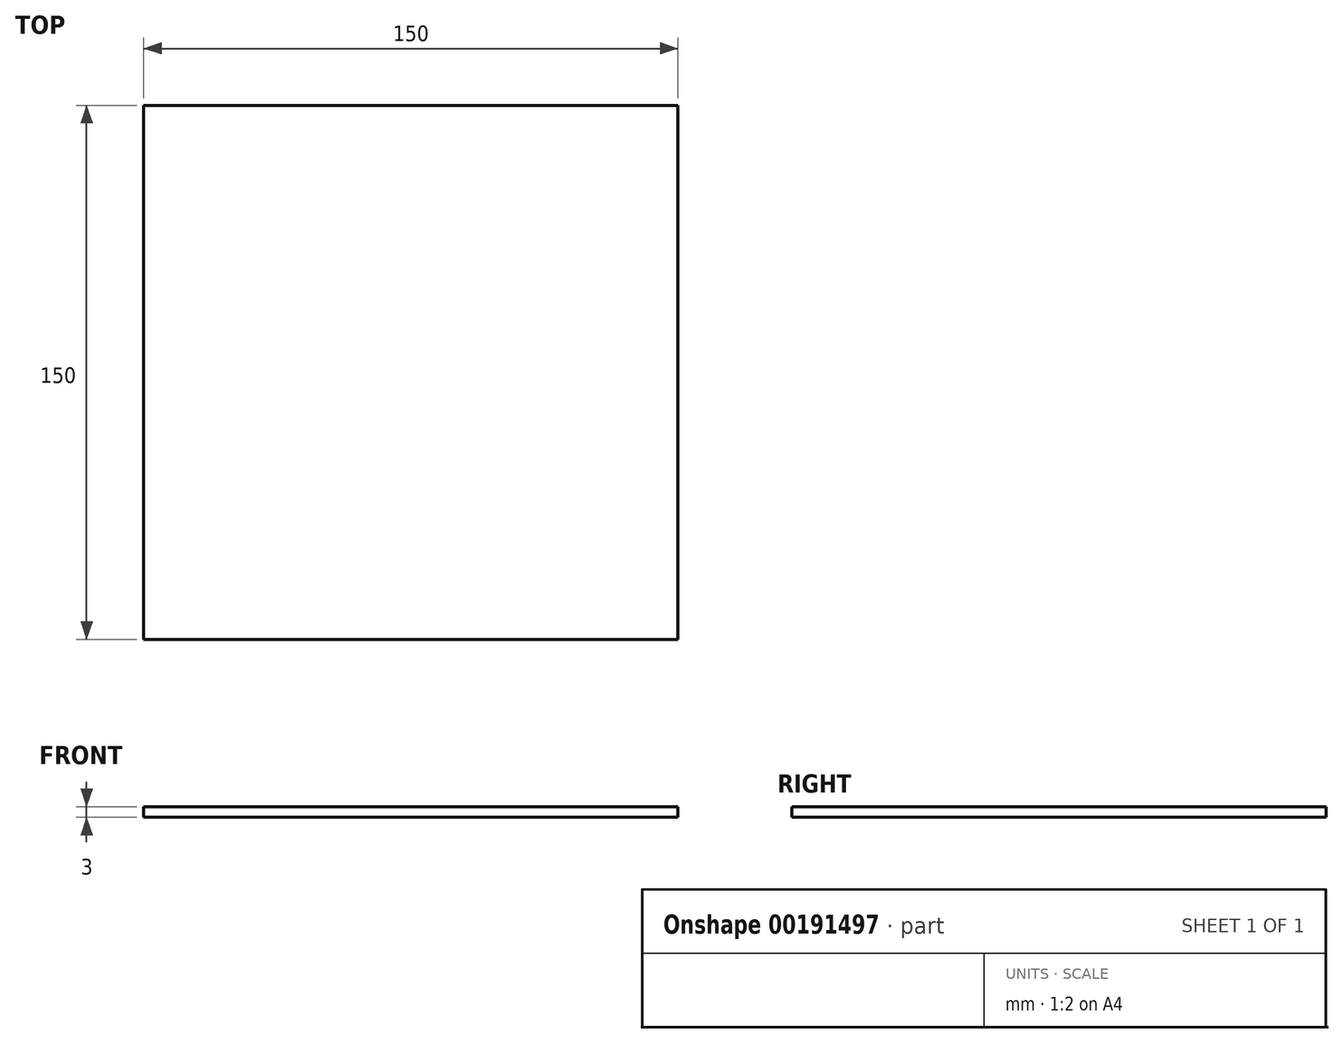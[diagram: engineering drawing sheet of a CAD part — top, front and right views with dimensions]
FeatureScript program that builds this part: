
annotation { "Feature Type Name" : "Feature", "Feature Type Description" : "" }
export const myFeature = defineFeature(function(context is Context, id is Id, definition is map)
    precondition{}
    {
        {
            var Q0;
            Q0=qCreatedBy(makeId("Top.planeOp"),FACE);
            var sketch = newSketch(context, id + "F0", { "sketchPlane" : qUnion([Q0])});
            skLineSegment(sketch, "E0.bottom", {"start": v(-75, 75) * mm, "end": v(75, 75) * mm});
            skLineSegment(sketch, "E0.top", {"start": v(-75, -75) * mm, "end": v(75, -75) * mm});
            skLineSegment(sketch, "E0.left", {"start": v(-75, 75) * mm, "end": v(-75, -75) * mm});
            skLineSegment(sketch, "E0.right", {"start": v(75, 75) * mm, "end": v(75, -75) * mm});
            skLineSegment(sketch, "E1", {"start": v(-75, -40) * mm, "end": v(75, -40) * mm});
            skLineSegment(sketch, "E2", {"start": v(75, -65) * mm, "end": v(-75, -65) * mm});
            skLineSegment(sketch, "E3", {"start": v(75, -28) * mm, "end": v(-75, -28) * mm});
            skSolve(sketch);
        }
        {
            var Q0;
            Q0=qSketchRegion(id+"F0",true);
            extrude(context, id + "F1", {"entities" : qUnion([Q0]), "depth" : 3 * mm});
        }
        {
            var Q0;
            Q0=makeQuery(id+"F1.opExtrude","SWEPT_FACE",FACE,{"disambiguationData":[OSD([sQuery(id+"F0.wireOp",EDGE,"E0.top")])]});
            var sketch = newSketch(context, id + "F2", { "sketchPlane" : qUnion([Q0])});
            skLineSegment(sketch, "E4.bottom", {"start": v(-75, 3) * mm, "end": v(75, 3) * mm});
            skLineSegment(sketch, "E4.top", {"start": v(-75, 103) * mm, "end": v(75, 103) * mm});
            skLineSegment(sketch, "E4.left", {"start": v(-75, 3) * mm, "end": v(-75, 103) * mm});
            skLineSegment(sketch, "E4.right", {"start": v(75, 3) * mm, "end": v(75, 103) * mm});
            skLineSegment(sketch, "E5", {"start": v(0, 3) * mm, "end": v(0, 103) * mm});
            skLineSegment(sketch, "E6", {"start": v(-50, 103) * mm, "end": v(-65, 3) * mm});
            skLineSegment(sketch, "E7", {"start": v(-25, 103) * mm, "end": v(-10, 3) * mm});
            skLineSegment(sketch, "E8", {"start": v(25, 103) * mm, "end": v(10, 3) * mm});
            skLineSegment(sketch, "E9", {"start": v(50, 103) * mm, "end": v(65, 3) * mm});
            skLineSegment(sketch, "E10", {"start": v(-62.98, 3) * mm, "end": v(-50.98, 83) * mm});
            skLineSegment(sketch, "E11", {"start": v(-12.02, 3) * mm, "end": v(-24.02, 83) * mm});
            skLineSegment(sketch, "E12", {"start": v(12.02, 3) * mm, "end": v(24.02, 83) * mm});
            skLineSegment(sketch, "E13", {"start": v(62.98, 3) * mm, "end": v(50.98, 83) * mm});
            skFitSpline(sketch, "E14", {"points": [v(-50.98, 83) * mm, v(-37.5, 99) * mm, v(-24.02, 83) * mm], "startDerivative": vector(32.87, 84) * mm, "endDerivative": vector(32.87, -84) * mm});
            skFitSpline(sketch, "E15", {"points": [v(24.02, 83) * mm, v(37.5, 99) * mm, v(50.98, 83) * mm], "startDerivative": vector(32.87, 84) * mm, "endDerivative": vector(32.87, -84) * mm});
            skSolve(sketch);
        }
        {
            var Q0;
            Q0=makeQuery(id+"F1.opExtrude","CAP_FACE",FACE,{"disambiguationData":[OSD([sQuery(id+"F0.wireOp",EDGE,"E0.bottom"),sQuery(id+"F0.wireOp",EDGE,"E0.top"),sQuery(id+"F0.wireOp",EDGE,"E0.left"),sQuery(id+"F0.wireOp",EDGE,"E0.right")])],"isStart":true});
            var sketch = newSketch(context, id + "F3", { "sketchPlane" : qUnion([Q0])});
            skText(sketch, "E16", { "text": "Nerf Triad/Jolt\nDual Holder\nRev. 1\nFLV - 07/2016", "fontName": "OpenSans-Bold.ttf"});
            const initialGuessF3  = {"E16": [-0.065, 0.01203, 1, 0, 0.01297]};
            skSetInitialGuess(sketch, initialGuessF3);
            skSolve(sketch);
        }
        {
            var Q0;
            Q0=sQuery(id+"F0.wireOp",EDGE,"E2");
            cPlane(context, id + "F4", {"entities" : qUnion([Q0]), "cplaneType" : CPlaneType.LINE_ANGLE, "offset" : 25 * mm, "angle" : 5 * degree, "width" : 150 * mm, "height" : 150 * mm});
        }
    });
